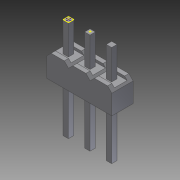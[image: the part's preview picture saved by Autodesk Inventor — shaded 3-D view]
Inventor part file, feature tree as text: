
AUTODESK INVENTOR PART (.ipt)
format: ipt  version: 2014 (Build 180170000, 170)  size: 107,008 bytes
history: native  units: mm (DEFAULTED — no unit token found)
features: other x2, sketch x1
ambient origin geometry x8: Origin, YZ Plane, XZ Plane, XY Plane, X Axis, Y Axis, Z Axis, Center Point
bodies: Volumenkörper1 (feature_tree)
feature tree (3):
  sketch  "Skizze1"
  other  "Arbeitspunkt1"
  other  "Arbeitspunkt2"
